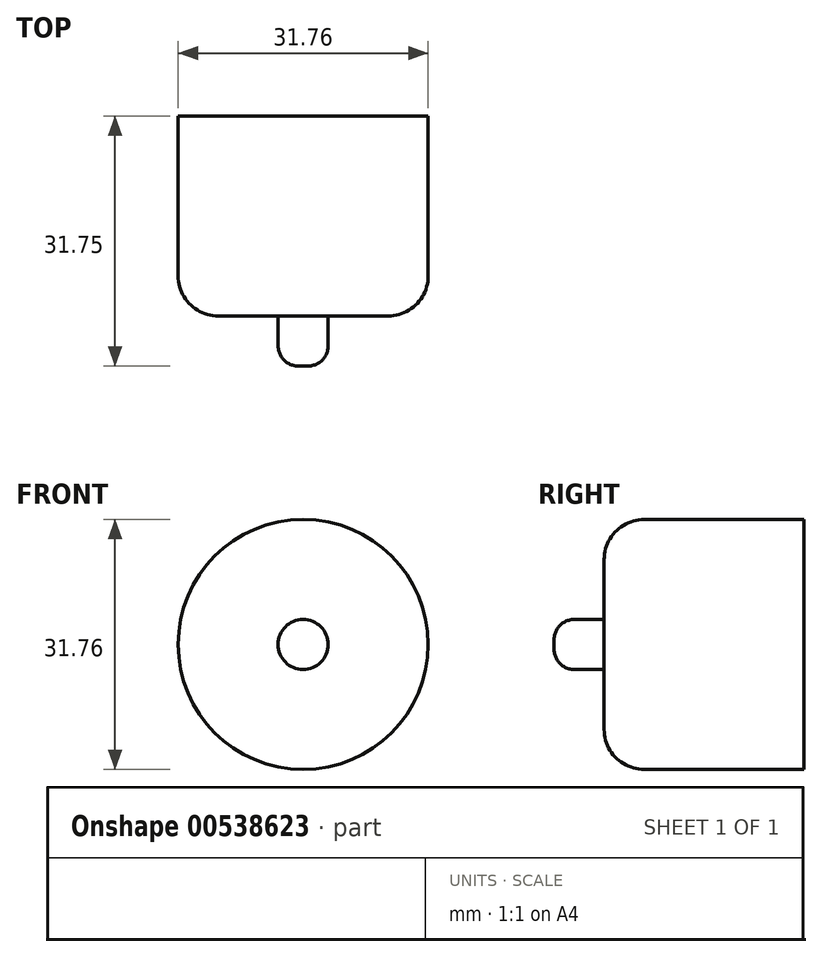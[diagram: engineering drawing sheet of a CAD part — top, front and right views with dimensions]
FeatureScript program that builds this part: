
annotation { "Feature Type Name" : "Feature", "Feature Type Description" : "" }
export const myFeature = defineFeature(function(context is Context, id is Id, definition is map)
    precondition{}
    {
        {
            var Q0;
            Q0=qCreatedBy(makeId("Front.planeOp"),FACE);
            var sketch = newSketch(context, id + "F0", { "sketchPlane" : qUnion([Q0])});
            skCircle(sketch, "E0", {"center": v(0, 0) * mm, "radius": 15.88 * mm});
            skSolve(sketch);
        }
        {
            var Q0;
            Q0 = qSketchRegion(id + "F0", true);
            extrude(context, id + "F1", {"entities" : qUnion([Q0]), "depth" : 25.4 * mm, "offsetDistance" : 25.4 * mm});
        }
        {
            var Q0;
            Q0=makeQuery(id+"F1.opExtrude","CAP_EDGE",EDGE,{"disambiguationData":[OSD([sQuery(id+"F0.wireOp",EDGE,"E0")])],"isStart":false});
            fillet(context, id + "F2", {"entities" : qUnion([Q0]), "radius" : 5.08 * mm, "tangentPropagation" : true, "allowEdgeOverflow" : false});
        }
        {
            var Q0;
            Q0=makeQuery(id+"F1.opExtrude","CAP_FACE",FACE,{"disambiguationData":[OSD([sQuery(id+"F0.wireOp",EDGE,"E0")])],"isStart":false});
            var sketch = newSketch(context, id + "F3", { "sketchPlane" : qUnion([Q0])});
            skCircle(sketch, "E1", {"center": v(0, 0) * mm, "radius": 3.18 * mm});
            skSolve(sketch);
        }
        {
            var Q0;
            Q0 = qSketchRegion(id + "F3", true);
            extrude(context, id + "F4", {"entities" : qUnion([Q0]), "operationType" : NewBodyOperationType.ADD, "depth" : 6.35 * mm, "offsetDistance" : 25.4 * mm});
        }
        {
            var Q0;
            Q0=makeQuery(id+"F4.opExtrude","CAP_EDGE",EDGE,{"disambiguationData":[OSD([sQuery(id+"F3.wireOp",EDGE,"E1")])],"isStart":false});
            var Q1;
            Q1=makeQuery(id+"F4.opExtrude","CAP_EDGE",EDGE,{"disambiguationData":[OSD([sQuery(id+"F3.wireOp",EDGE,"E1")])],"isStart":true});
            fillet(context, id + "F5", {"entities" : qUnion([Q0, Q1]), "radius" : 2.54 * mm, "tangentPropagation" : true, "allowEdgeOverflow" : false});
        }
    });
